# Revit family: Seating_Inc-Hover_Square
name_source: partatom
category: Furniture
revit_build: Autodesk Revit MEP 2014 (Build: 20130308_1515(x64)
units: mm (PartAtom-declared; Revit-internal decimal feet)

## types (6) — shared parameters
Assembly Code = E2020200
Keynote = 12500
Leg = STI - Plastic
Manufacturer = seating inc.
Seat = STI - Fabric
URL = http://www.seatinginc.com

## per-type parameters (varying)
| type | Depth | Description | Height | Model | Type Comments | Width |
| Hover-Square HP18S | 18" | Hover Square 18"W 18"D 18"H | 18" | HP18S | Hover Square | 18" |
| Hover-Square HP24S | 24" | Hover Square 24"W 24"D 18"H | 18" | HP24S | Hover Square | 24" |
| Hover-Square HP30S | 30" | Hover Square 30"W 30"D 18"H | 18" | HP30S | Hover Square | 30" |
| Hover-Mini Square HM18S | 18" | Hover Mini Square 18"W 18"D 15"H | 15" | HM18S | Hover Mini Square | 18" |
| Hover-Mini Square HM24S | 24" | Hover Mini Square 24"W 24"D 15"H | 15" | HM24S | Hover Mini Square | 24" |
| Hover-Mini Square HM30S | 30" | Hover Mini Square 30"W 30"D 15"H | 15" | HM30S | Hover Mini Square | 30" |

## geometry (parser evidence)
native form markers: Sweep x1
no freeform markers — native parametric forms only
